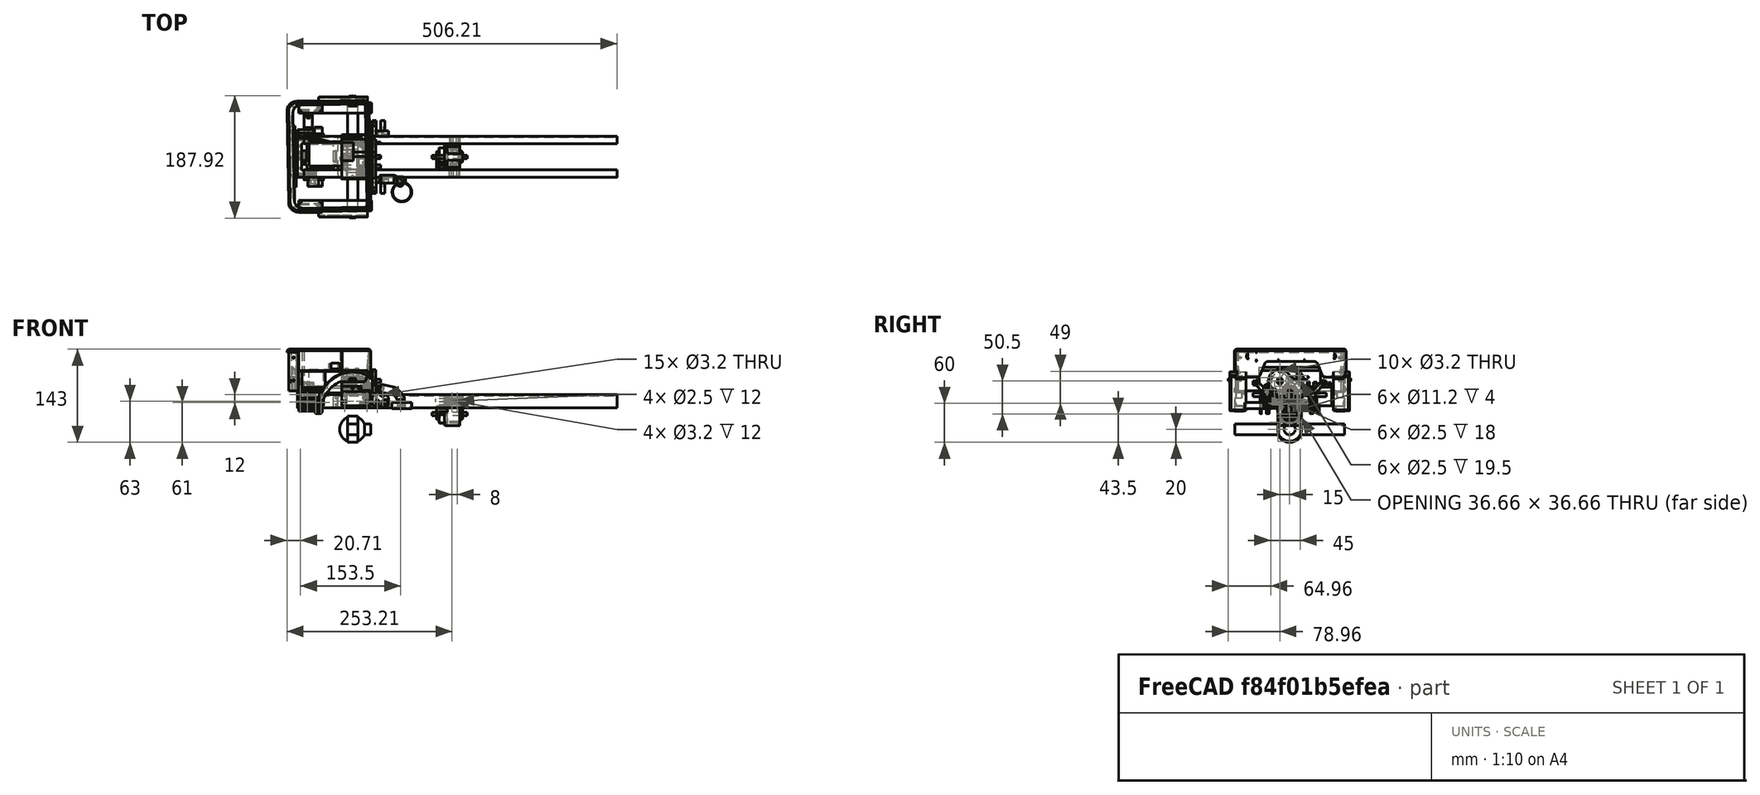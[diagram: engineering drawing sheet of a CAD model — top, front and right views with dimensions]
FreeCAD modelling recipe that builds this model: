
FCSTD DOCUMENT  (FreeCAD 0.18.4R)
Label: gearbox-01
License: All rights reserved
LicenseURL: http://en.wikipedia.org/wiki/All_rights_reserved
objects: Part::Cylinder×79, Part::MultiFuse×46, Part::Cut×41, Part::Box×25, Part::Fillet×25, Part::Chamfer×11, Part::Feature×6, Part::Extrusion×5, Part::Mirroring×4, Part::Sphere×1
note: 243 computed .brp shape members not serialized (recipe doc carries the construction recipe); baked Part::Feature solids carry a one-line shape summary decoded from their .brp

FEATURE [Part::Box] Box416  label="Cube641"
  AttacherType = Attacher::AttachEngine3D
  Height = 20
  Length = 480
  Placement = pos=(0,0,-92) rot=(0,0,1;0rad)
  Width = 11.5
FEATURE [Part::Box] Box417  label="Cube642"
  AttacherType = Attacher::AttachEngine3D
  Height = 17
  Length = 480
  Placement = pos=(0,1.5,-90.5) rot=(0,0,1;0rad)
  Width = 10
FEATURE [Part::Cut] Cut429  label="Cut768"
  Base = -> Box416
  Refine = true
  Tool = -> Box417
FEATURE [Part::Fillet] Fillet268
  Base = -> Cut429
  Edges = 2 edges r=3: [Edge11,Edge23]
  Placement = pos=(0,-1.5,0) rot=(0,0,1;0rad)
FEATURE [Part::Box] Box418  label="Cube643"
  AttacherType = Attacher::AttachEngine3D
  Height = 20
  Length = 480
  Placement = pos=(0,0,-92) rot=(0,0,1;0rad)
  Width = 11.5
FEATURE [Part::Box] Box419  label="Cube644"
  AttacherType = Attacher::AttachEngine3D
  Height = 17
  Length = 480
  Placement = pos=(0,1.5,-90.5) rot=(0,0,1;0rad)
  Width = 10
FEATURE [Part::Cut] Cut430  label="Cut769"
  Base = -> Box418
  Refine = true
  Tool = -> Box419
FEATURE [Part::Fillet] Fillet269
  Base = -> Cut430
  Edges = 2 edges r=3: [Edge11,Edge23]
FEATURE [Part::Mirroring] Part__Mirroring036  label="Fillet269 (Mirror #29)"
  Base = (0,0,0)
  Normal = (0,1,0)
  Placement = pos=(0,61.5,0) rot=(0,0,1;0rad)
  Source = -> Fillet269
FEATURE [Part::MultiFuse] Fusion231  label="frame-00"
  Placement = pos=(23.5,55,74) rot=(0,0,1;0rad)
  Refine = true
  Shapes = -> [Part__Mirroring036,Fillet268]
FEATURE [Part::Box] Box042  label="Cube280"
  AttacherType = Attacher::AttachEngine3D
  Height = 28
  Length = 21
  Placement = pos=(-13,0,0) rot=(0,0,1;0rad)
  Width = 170
FEATURE [Part::Fillet] Fillet013
  Base = -> Box042
  Edges = 2 edges r=15: [Edge1,Edge3]
FEATURE [Part::Box] Box184  label="Cube410"
  AttacherType = Attacher::AttachEngine3D
  Height = 10
  Length = 2.5
  Placement = pos=(-1.25,0,0) rot=(0,0,1;0rad)
  Width = 4
FEATURE [Part::Cylinder] Cylinder068
  Angle = 360
  AttacherType = Attacher::AttachEngine3D
  Height = 10
  Placement = pos=(0,4,0) rot=(0,0,1;0rad)
  Radius = 1.25
FEATURE [Part::Cylinder] Cylinder069
  Angle = 360
  AttacherType = Attacher::AttachEngine3D
  Height = 10
  Radius = 1.25
FEATURE [Part::MultiFuse] Fusion056
  Placement = pos=(0,8,0) rot=(0,0,1;0rad)
  Refine = true
  Shapes = -> [Box184,Cylinder068,Cylinder069]
FEATURE [Part::Cut] Cut014047  label="diff-box-rear-01"
  Placement = pos=(0,0,-1) rot=(0,0,1;0rad)
  Refine = true
FEATURE [Part::Fillet] Fillet355  label="diff-box-front-01"
  Edges = 1 edges r=1.99: [Edge305]
FEATURE [Part::Cylinder] Cylinder088
  Angle = 360
  AttacherType = Attacher::AttachEngine3D
  Height = 43.5
  Placement = pos=(20.75,0,-18.5) rot=(0,0,1;0rad)
  Radius = 2.5
FEATURE [Part::Cylinder] Cylinder087
  Angle = 360
  AttacherType = Attacher::AttachEngine3D
  Height = 54
  Placement = pos=(0,0,-23.5) rot=(0,0,1;0rad)
  Radius = 2.5
FEATURE [Part::Cut] Cut014020  label="diff-box-mount-left"
  Base = -> Fillet013
  Placement = pos=(0,0,-1) rot=(0,0,1;0rad)
  Refine = true
  Tool = -> Fusion056
FEATURE [Part::Mirroring] Part__Mirroring001  label="diff-box-mount-right"
  Base = (0,0,0)
  Normal = (0,1,0)
  Placement = pos=(0,0,-1) rot=(0,0,1;0rad)
FEATURE [Part::MultiFuse] Fusion514  label="transfer-case"
  Placement = pos=(250,85,-27.5) rot=(0,-1,0;1.5708rad)
  Refine = true
  Shapes = -> [Cut014047,Fillet355,Cylinder087,Cylinder088,Cut014020,Part__Mirroring001]
FEATURE [Part::Fillet] Fillet357  label="steering-servo-rear-mount"
  Edges = 4 edges r=3: [Edge11,Edge13,Edge21,Edge23]
  Placement = pos=(1,0,3) rot=(0,0,1;0rad)
FEATURE [Part::Cut] Cut694  label="steering-servo-front-mount"
  Placement = pos=(0,0,3) rot=(0,0,1;0rad)
  Refine = true
FEATURE [Part::MultiFuse] Fusion588  label="steering-servo"
  Placement = pos=(1,0,3) rot=(0,0,1;0rad)
  Refine = true
FEATURE [Part::Cut] Cut688  label="servo-shaft-coupler"
  Placement = pos=(37,58.75,-14.35) rot=(1,0,0;1.5708rad)
  Refine = true
FEATURE [Part::Box] Box498  label="Cube700"
  AttacherType = Attacher::AttachEngine3D
  Height = 16
  Length = 16
  Placement = pos=(90,1,-59) rot=(0,0,1;0rad)
  Width = 168
FEATURE [Part::Cylinder] Cylinder793  label="Cylinder955"
  Angle = 360
  AttacherType = Attacher::AttachEngine3D
  Height = 16
  Placement = pos=(90,85,-51) rot=(0,1,0;1.5708rad)
  Radius = 20
FEATURE [Part::Sphere] Sphere
  Angle1 = -90
  Angle2 = 90
  Angle3 = 360
  AttacherType = Attacher::AttachEngine3D
  Placement = pos=(98,85,-51) rot=(0,0,1;0rad)
  Radius = 20
FEATURE [Part::Cylinder] Cylinder794  label="Cylinder956"
  Angle = 360
  AttacherType = Attacher::AttachEngine3D
  Height = 28
  Placement = pos=(98,85,-51) rot=(0,1,0;1.5708rad)
  Radius = 8.5
FEATURE [Part::MultiFuse] Fusion512  label="front-axle"
  Refine = true
  Shapes = -> [Box498,Sphere,Cylinder794,Cylinder793]
FEATURE [Part::Cylinder] Cylinder
  Angle = 360
  AttacherType = Attacher::AttachEngine3D
  Height = 39.5
  Placement = pos=(0,0,23) rot=(0,1,0;1.5708rad)
  Radius = 13
FEATURE [Part::Cylinder] Cylinder795
  Angle = 360
  AttacherType = Attacher::AttachEngine3D
  Height = 39.5
  Placement = pos=(0,0,0) rot=(0,1,0;1.5708rad)
  Radius = 19.5
FEATURE [Part::Cylinder] Cylinder798  label="cylinder"
  Angle = 360
  AttacherType = Attacher::AttachEngine3D
  Height = 50
  Placement = pos=(31,89,23) rot=(0,1,0;1.5708rad)
  Radius = 18
FEATURE [Part::MultiFuse] Fusion  label="gearbox002"
  Placement = pos=(89,84.9373,3.51066) rot=(1,0,0;0.706858rad)
  Refine = true
  Shapes = -> [Cylinder,Cylinder795]
FEATURE [Part::Box] Box  label="Cube"
  AttacherType = Attacher::AttachEngine3D
  Height = 41
  Length = 47.5
  Placement = pos=(81,65,-17) rot=(0,0,1;0rad)
  Width = 40
FEATURE [Part::Cylinder] Cylinder799
  Angle = 360
  AttacherType = Attacher::AttachEngine3D
  Height = 60
  Placement = pos=(81,85,3.5) rot=(0,1,0;1.5708rad)
  Radius = 2.5
FEATURE [Part::Cylinder] Cylinder800
  Angle = 360
  AttacherType = Attacher::AttachEngine3D
  Height = 60
  Placement = pos=(81,70,21) rot=(0,1,0;1.5708rad)
  Radius = 2.5
FEATURE [Part::MultiFuse] Fusion590
  Refine = true
  Shapes = -> [Cylinder799,Cylinder800]
FEATURE [Part::Cylinder] Cylinder801  label="main-motor001"
  Angle = 360
  AttacherType = Attacher::AttachEngine3D
  Height = 18
  Placement = pos=(81,89,21) rot=(0,1,0;1.5708rad)
  Radius = 18
FEATURE [Part::Cylinder] Cylinder802
  Angle = 360
  AttacherType = Attacher::AttachEngine3D
  Height = 47.5
  Placement = pos=(81,70,21) rot=(0,1,0;1.5708rad)
  Radius = 17.5
FEATURE [Part::Cylinder] Cylinder804
  Angle = 360
  AttacherType = Attacher::AttachEngine3D
  Height = 60
  Placement = pos=(81,106.419,11.8645) rot=(0.034878,0.998783,0.034878;1.57201rad)
  Radius = 1.5
FEATURE [Part::Feature] Fillet007001  label="selector"
  Placement = pos=(119.5,85,5.5) rot=(0.181732,-0.966409,-0.181732;1.60496rad)
  shape: bbox 10 x 30 x 28.57 mm, 21 faces (baked)
FEATURE [Part::Box] Box499  label="Cube701"
  AttacherType = Attacher::AttachEngine3D
  Height = 22
  Length = 47.5
  Placement = pos=(81,105,2) rot=(0,0,1;0rad)
  Width = 7
FEATURE [Part::MultiFuse] Fusion591
  Refine = true
  Shapes = -> [Box499,Cylinder802,Box,Cylinder801]
FEATURE [Part::Cylinder] Cylinder805
  Angle = 360
  AttacherType = Attacher::AttachEngine3D
  Height = 10
  Placement = pos=(89,70,21) rot=(0,1,0;1.5708rad)
  Radius = 16.5
FEATURE [Part::MultiFuse] Fusion592
  Refine = true
  Shapes = -> [Fusion,Cylinder805]
FEATURE [Part::Cut] Cut
  Base = -> Fusion591
  Refine = true
  Tool = -> Fusion592
FEATURE [Part::Chamfer] Chamfer
  Base = -> Cut
  Edges = 1 edges r=3.49: [Edge39]
FEATURE [Part::Fillet] Fillet
  Base = -> Chamfer
  Edges = 1 edges r=3: [Edge25]
FEATURE [Part::Fillet] Fillet007002
  Base = -> Fillet
  Edges = 2 edges r=6: [Edge13,Edge18]
FEATURE [Part::Box] Box500  label="Cube702"
  AttacherType = Attacher::AttachEngine3D
  Height = 20
  Length = 60
  Placement = pos=(81,53.25,-18) rot=(0,0,1;0rad)
  Width = 63.5
FEATURE [Part::Feature] Face
  shape: bbox 2.621e-05 x 37.61 x 40.07 mm, 1 faces, 0 solids (baked)
FEATURE [Part::Extrusion] Extrude
  Base = -> Face
  Dir = (60,0,0)
  DirMode = 0
  FaceMakerClass = Part::FaceMakerExtrusion
  LengthFwd = 0
  LengthRev = 0
  Placement = pos=(-30.4,1.43133,-5.60163) rot=(1,0,0;0.069813rad)
  Solid = false
  Symmetric = false
FEATURE [Part::Cylinder] Cylinder806
  Angle = 360
  AttacherType = Attacher::AttachEngine3D
  Height = 60
  Placement = pos=(81,106.419,11.8645) rot=(0.034878,0.998783,0.034878;1.57201rad)
  Radius = 3.1
FEATURE [Part::Cut] Cut014049
  Base = -> Fillet007002
  Refine = true
  Tool = -> Extrude
FEATURE [Part::Cut] Cut014050
  Base = -> Cut014049
  Refine = true
  Tool = -> Cylinder806
FEATURE [Part::Cylinder] Cylinder807  label="Cylinder000"
  Angle = 360
  AttacherType = Attacher::AttachEngine3D
  Height = 50
  Placement = pos=(45,89,21) rot=(0,1,0;1.5708rad)
  Radius = 7
FEATURE [Part::Cut] Cut014051
  Base = -> Cut014050
  Refine = true
  Tool = -> Cylinder807
FEATURE [Part::Chamfer] Chamfer109
  Base = -> Cut014051
  Edges = 1 edges r=5.2: [Edge52]
FEATURE [Part::Cylinder] Cylinder808  label="Cylinder957"
  Angle = 360
  AttacherType = Attacher::AttachEngine3D
  Height = 50
  Placement = pos=(56,89,33.5) rot=(0,1,0;1.5708rad)
  Radius = 1.6
FEATURE [Part::Cylinder] Cylinder809  label="Cylinder958"
  Angle = 360
  AttacherType = Attacher::AttachEngine3D
  Height = 50
  Placement = pos=(56,89,8.5) rot=(0,1,0;1.5708rad)
  Radius = 1.6
FEATURE [Part::MultiFuse] Fusion593
  Placement = pos=(0,14.7618,74.3919) rot=(-1,0,0;0.855211rad)
  Refine = true
  Shapes = -> [Cylinder808,Cylinder809]
FEATURE [Part::Cylinder] Cylinder810  label="Cylinder959"
  Angle = 360
  AttacherType = Attacher::AttachEngine3D
  Height = 15
  Placement = pos=(56,89,33.5) rot=(0,1,0;1.5708rad)
  Radius = 3.1
FEATURE [Part::Cylinder] Cylinder811  label="Cylinder960"
  Angle = 360
  AttacherType = Attacher::AttachEngine3D
  Height = 15
  Placement = pos=(56,89,8.5) rot=(0,1,0;1.5708rad)
  Radius = 3.1
FEATURE [Part::MultiFuse] Fusion594
  Placement = pos=(28,14.7618,74.3919) rot=(-1,0,0;0.855211rad)
  Refine = true
  Shapes = -> [Cylinder810,Cylinder811]
FEATURE [Part::MultiFuse] Fusion595
  Refine = true
  Shapes = -> [Fusion593,Fusion594]
FEATURE [Part::Cut] Cut014052
  Base = -> Chamfer109
  Refine = true
  Tool = -> Fusion595
FEATURE [Part::Cylinder] Cylinder812
  Angle = 360
  AttacherType = Attacher::AttachEngine3D
  Height = 60
  Placement = pos=(81,85,3.5) rot=(0,1,0;1.5708rad)
  Radius = 5.6
FEATURE [Part::Cylinder] Cylinder813
  Angle = 360
  AttacherType = Attacher::AttachEngine3D
  Height = 60
  Placement = pos=(81,70,21) rot=(0,1,0;1.5708rad)
  Radius = 5.6
FEATURE [Part::MultiFuse] Fusion596
  Placement = pos=(4,0,0) rot=(0,0,1;0rad)
  Refine = true
  Shapes = -> [Cylinder812,Cylinder813]
FEATURE [Part::Cylinder] Cylinder814
  Angle = 360
  AttacherType = Attacher::AttachEngine3D
  Height = 60
  Placement = pos=(81,85,3.5) rot=(0,1,0;1.5708rad)
  Radius = 4
FEATURE [Part::Cylinder] Cylinder815
  Angle = 360
  AttacherType = Attacher::AttachEngine3D
  Height = 60
  Placement = pos=(81,70,21) rot=(0,1,0;1.5708rad)
  Radius = 4
FEATURE [Part::MultiFuse] Fusion597
  Refine = true
  Shapes = -> [Cylinder814,Cylinder815]
FEATURE [Part::MultiFuse] Fusion598
  Refine = true
  Shapes = -> [Fusion596,Fusion597]
FEATURE [Part::Cut] Cut014053
  Base = -> Cut014052
  Refine = true
  Tool = -> Fusion598
FEATURE [Part::Cylinder] Cylinder816
  Angle = 360
  AttacherType = Attacher::AttachEngine3D
  Height = 20
  Placement = pos=(81,69,-13) rot=(0,1,0;1.5708rad)
  Radius = 1.25
FEATURE [Part::Cylinder] Cylinder817
  Angle = 360
  AttacherType = Attacher::AttachEngine3D
  Height = 20
  Placement = pos=(81,101,-13) rot=(0,1,0;1.5708rad)
  Radius = 1.25
FEATURE [Part::Cylinder] Cylinder818
  Angle = 360
  AttacherType = Attacher::AttachEngine3D
  Height = 20
  Placement = pos=(81,101,21) rot=(0,1,0;1.5708rad)
  Radius = 1.25
FEATURE [Part::Cylinder] Cylinder819
  Angle = 360
  AttacherType = Attacher::AttachEngine3D
  Height = 20
  Placement = pos=(81,70,36) rot=(0,1,0;1.5708rad)
  Radius = 1.25
FEATURE [Part::Cylinder] Cylinder820
  Angle = 360
  AttacherType = Attacher::AttachEngine3D
  Height = 20
  Placement = pos=(81,56,26) rot=(0,1,0;1.5708rad)
  Radius = 1.25
FEATURE [Part::Cylinder] Cylinder821
  Angle = 360
  AttacherType = Attacher::AttachEngine3D
  Height = 20
  Placement = pos=(81,62,8) rot=(0,1,0;1.5708rad)
  Radius = 1.25
FEATURE [Part::MultiFuse] Fusion599
  Placement = pos=(28,0,0) rot=(0,0,1;0rad)
  Refine = true
  Shapes = -> [Cylinder816,Cylinder820,Cylinder821,Cylinder817,Cylinder818,Cylinder819]
FEATURE [Part::Cut] Cut014054
  Base = -> Cut014053
  Placement = pos=(0,0,2) rot=(0,0,1;0rad)
  Refine = true
  Tool = -> Fusion599
FEATURE [Part::Box] Box501  label="Cube703"
  AttacherType = Attacher::AttachEngine3D
  Height = 22
  Length = 44
  Placement = pos=(81,51,-15) rot=(0,0,1;0rad)
  Width = 14
FEATURE [Part::Fillet] Fillet007003
  Base = -> Box500
  Edges = 2 edges r=3: [Edge10,Edge12]
FEATURE [Part::Box] Box502  label="Cube704"
  AttacherType = Attacher::AttachEngine3D
  Height = 22
  Length = 44
  Placement = pos=(81,105,-15) rot=(0,0,1;0rad)
  Width = 14
FEATURE [Part::Cylinder] Cylinder822  label="Cylinder961"
  Angle = 360
  AttacherType = Attacher::AttachEngine3D
  Height = 5
  Placement = pos=(120,125,-8) rot=(1,0,0;1.5708rad)
  Radius = 1.6
FEATURE [Part::Cylinder] Cylinder823  label="Cylinder962"
  Angle = 360
  AttacherType = Attacher::AttachEngine3D
  Height = 5
  Placement = pos=(86,125,-8) rot=(1,0,0;1.5708rad)
  Radius = 1.6
FEATURE [Part::MultiFuse] Fusion603
  Placement = pos=(0,-5,0) rot=(0,0,1;0rad)
  Refine = true
  Shapes = -> [Cylinder823,Cylinder822]
FEATURE [Part::Cylinder] Cylinder824  label="Cylinder963"
  Angle = 360
  AttacherType = Attacher::AttachEngine3D
  Height = 5
  Placement = pos=(120,125,-8) rot=(1,0,0;1.5708rad)
  Radius = 1.6
FEATURE [Part::Cylinder] Cylinder825  label="Cylinder964"
  Angle = 360
  AttacherType = Attacher::AttachEngine3D
  Height = 5
  Placement = pos=(86,125,-8) rot=(1,0,0;1.5708rad)
  Radius = 1.6
FEATURE [Part::MultiFuse] Fusion604
  Placement = pos=(0,-70,0) rot=(0,0,1;0rad)
  Refine = true
  Shapes = -> [Cylinder825,Cylinder824]
FEATURE [Part::MultiFuse] Fusion605
  Refine = true
  Shapes = -> [Fusion603,Fusion604]
FEATURE [Part::Feature] Face044
  shape: bbox 2e-07 x 80.32 x 83.91 mm, 1 faces, 0 solids (baked)
FEATURE [Part::Extrusion] Extrude001
  Base = -> Face044
  Dir = (5,0,0)
  DirMode = 0
  FaceMakerClass = Part::FaceMakerExtrusion
  LengthFwd = 0
  LengthRev = 0
  Solid = false
  Symmetric = false
FEATURE [Part::Cylinder] Cylinder826
  Angle = 360
  AttacherType = Attacher::AttachEngine3D
  Height = 60
  Placement = pos=(81,85,3.5) rot=(0,1,0;1.5708rad)
  Radius = 4
FEATURE [Part::Cylinder] Cylinder827
  Angle = 360
  AttacherType = Attacher::AttachEngine3D
  Height = 60
  Placement = pos=(81,70,21) rot=(0,1,0;1.5708rad)
  Radius = 4
FEATURE [Part::MultiFuse] Fusion606
  Refine = true
  Shapes = -> [Cylinder826,Cylinder827]
FEATURE [Part::Cylinder] Cylinder828
  Angle = 360
  AttacherType = Attacher::AttachEngine3D
  Height = 60
  Placement = pos=(81,85,3.5) rot=(0,1,0;1.5708rad)
  Radius = 5.6
FEATURE [Part::Cylinder] Cylinder829
  Angle = 360
  AttacherType = Attacher::AttachEngine3D
  Height = 60
  Placement = pos=(81,70,21) rot=(0,1,0;1.5708rad)
  Radius = 5.6
FEATURE [Part::MultiFuse] Fusion607
  Placement = pos=(-8.5,0,0) rot=(0,0,1;0rad)
  Refine = true
  Shapes = -> [Cylinder828,Cylinder829]
FEATURE [Part::MultiFuse] Fusion608
  Refine = true
  Shapes = -> [Fusion607,Fusion606]
FEATURE [Part::Cut] Cut014057
  Base = -> Extrude001
  Refine = true
  Tool = -> Fusion608
FEATURE [Part::Cylinder] Cylinder830
  Angle = 360
  AttacherType = Attacher::AttachEngine3D
  Height = 60
  Placement = pos=(81,106.419,11.8645) rot=(0.034878,0.998783,0.034878;1.57201rad)
  Radius = 3.1
FEATURE [Part::Cut] Cut014058
  Base = -> Cut014057
  Refine = true
  Tool = -> Cylinder830
FEATURE [Part::Cylinder] Cylinder831
  Angle = 360
  AttacherType = Attacher::AttachEngine3D
  Height = 20
  Placement = pos=(81,69,-13) rot=(0,1,0;1.5708rad)
  Radius = 1.6
FEATURE [Part::Cylinder] Cylinder832
  Angle = 360
  AttacherType = Attacher::AttachEngine3D
  Height = 20
  Placement = pos=(81,101,-13) rot=(0,1,0;1.5708rad)
  Radius = 1.6
FEATURE [Part::Cylinder] Cylinder833
  Angle = 360
  AttacherType = Attacher::AttachEngine3D
  Height = 20
  Placement = pos=(81,101,21) rot=(0,1,0;1.5708rad)
  Radius = 1.6
FEATURE [Part::Cylinder] Cylinder834
  Angle = 360
  AttacherType = Attacher::AttachEngine3D
  Height = 20
  Placement = pos=(81,70,36) rot=(0,1,0;1.5708rad)
  Radius = 1.6
FEATURE [Part::Cylinder] Cylinder835
  Angle = 360
  AttacherType = Attacher::AttachEngine3D
  Height = 20
  Placement = pos=(81,56,26) rot=(0,1,0;1.5708rad)
  Radius = 1.6
FEATURE [Part::Cylinder] Cylinder836
  Angle = 360
  AttacherType = Attacher::AttachEngine3D
  Height = 20
  Placement = pos=(81,62,8) rot=(0,1,0;1.5708rad)
  Radius = 1.6
FEATURE [Part::MultiFuse] Fusion609
  Placement = pos=(40,0,2) rot=(0,0,1;0rad)
  Refine = true
  Shapes = -> [Cylinder831,Cylinder835,Cylinder836,Cylinder832,Cylinder833,Cylinder834]
FEATURE [Part::Box] Box504  label="Cube706"
  AttacherType = Attacher::AttachEngine3D
  Height = 10
  Length = 30
  Placement = pos=(81,111,5) rot=(0,0,1;0rad)
  Width = 5.5
FEATURE [Part::MultiFuse] Fusion610  label="gearbox-rods"
  Placement = pos=(0,0,2) rot=(0,0,1;0rad)
  Refine = true
  Shapes = -> [Cylinder804,Fusion590]
FEATURE [Part::Chamfer] Chamfer110
  Base = -> Box502
  Edges = 1 edges r=2: [Edge10]
FEATURE [Part::MultiFuse] Fusion611
  Refine = true
  Shapes = -> [Box501,Chamfer110]
FEATURE [Part::Cut] Cut014060
  Base = -> Fusion611
  Refine = true
  Tool = -> Fillet007003
FEATURE [Part::MultiFuse] Fusion612
  Refine = true
  Shapes = -> [Cut014054,Cut014060]
FEATURE [Part::Fillet] Fillet007004
  Base = -> Fusion612
  Edges = 1 edges r=4: [Edge94]
FEATURE [Part::Fillet] Fillet007005
  Base = -> Fillet007004
  Edges = 2 edges r=4: [Edge124,Edge131]
FEATURE [Part::Chamfer] Chamfer111
  Base = -> Fillet007005
  Edges = 1 edges r=3: [Edge58]
FEATURE [Part::Fillet] Fillet007006
  Base = -> Chamfer111
  Edges = 1 edges r=2: [Edge92]
FEATURE [Part::Fillet] Fillet007007
  Base = -> Cut014058
  Edges = 1 edges r=2: [Edge1]
FEATURE [Part::Fillet] Fillet007008
  Base = -> Fillet007007
  Edges = 1 edges r=3: [Edge41]
  Placement = pos=(0,0,2) rot=(0,0,1;0rad)
FEATURE [Part::Fillet] Fillet007009
  Base = -> Fillet007006
  Edges = 1 edges r=2.99: [Edge67]
FEATURE [Part::Cylinder] Cylinder837  label="Cylinder965"
  Angle = 360
  AttacherType = Attacher::AttachEngine3D
  Height = 10
  Placement = pos=(96,125,-8) rot=(1,0,0;1.5708rad)
  Radius = 1.25
FEATURE [Part::Cylinder] Cylinder838  label="Cylinder966"
  Angle = 360
  AttacherType = Attacher::AttachEngine3D
  Height = 10
  Placement = pos=(86,125,-8) rot=(1,0,0;1.5708rad)
  Radius = 1.25
FEATURE [Part::MultiFuse] Fusion613
  Placement = pos=(12,-3.5,20) rot=(0,0,1;0rad)
  Refine = true
  Shapes = -> [Cylinder838,Cylinder837]
FEATURE [Part::Cylinder] Cylinder839  label="Cylinder967"
  Angle = 360
  AttacherType = Attacher::AttachEngine3D
  Height = 8
  Placement = pos=(96,124,-8) rot=(1,0,0;1.5708rad)
  Radius = 1.25
FEATURE [Part::Cylinder] Cylinder840  label="Cylinder968"
  Angle = 360
  AttacherType = Attacher::AttachEngine3D
  Height = 8
  Placement = pos=(86,120.5,-8) rot=(1,0,0;1.5708rad)
  Radius = 1.25
FEATURE [Part::Box] Box505  label="Cube707"
  AttacherType = Attacher::AttachEngine3D
  Height = 10
  Length = 30
  Placement = pos=(95,53.5,5) rot=(0,0,1;0rad)
  Width = 7
FEATURE [Part::Chamfer] Chamfer112
  Base = -> Box505
  Edges = 1 edges r=6: [Edge12]
  Placement = pos=(-14,0,0) rot=(0,0,1;0rad)
FEATURE [Part::Fillet] Fillet007010
  Base = -> Box504
  Edges = 1 edges r=1: [Edge12]
FEATURE [Part::Fillet] Fillet007011
  Base = -> Chamfer112
  Edges = 1 edges r=0.99: [Edge7]
FEATURE [Part::MultiFuse] Fusion616
  Refine = true
  Shapes = -> [Fillet007009,Fillet007011,Fillet007010]
FEATURE [Part::MultiFuse] Fusion614
  Placement = pos=(12,-64,20) rot=(0,0,1;0rad)
  Refine = true
  Shapes = -> [Cylinder840,Cylinder839]
FEATURE [Part::MultiFuse] Fusion617
  Refine = true
  Shapes = -> [Fusion613,Fusion614]
FEATURE [Part::MultiFuse] Fusion618
  Refine = true
  Shapes = -> [Fusion605,Fusion617]
FEATURE [Part::Fillet] Fillet007012
  Base = -> Fusion616
  Edges = 2 edges r=6: [Edge81,Edge92]
FEATURE [Part::Box] Box506  label="Cube708"
  AttacherType = Attacher::AttachEngine3D
  Height = 2
  Length = 39.5
  Placement = pos=(89,104,2) rot=(1,0,0;1.0821rad)
  Width = 10
FEATURE [Part::Box] Box507  label="Cube709"
  AttacherType = Attacher::AttachEngine3D
  Height = 2
  Length = 39.5
  Placement = pos=(89,96,19) rot=(-1,0,0;0.314159rad)
  Width = 10
FEATURE [Part::MultiFuse] Fusion619
  Refine = true
  Shapes = -> [Box507,Box506]
FEATURE [Part::Cut] Cut014062
  Base = -> Fillet007012
  Refine = true
  Tool = -> Fusion619
FEATURE [Part::Cylinder] Cylinder841
  Angle = 360
  AttacherType = Attacher::AttachEngine3D
  Height = 19
  Placement = pos=(89,70,23) rot=(0,1,0;1.5708rad)
  Radius = 16.5
FEATURE [Part::Chamfer] Chamfer113
  Base = -> Cylinder841
  Edges = 1 edges r=4: [Edge1]
FEATURE [Part::Box] Box508  label="Cube710"
  AttacherType = Attacher::AttachEngine3D
  Height = 32
  Length = 19
  Placement = pos=(89,70,7) rot=(0,0,1;0rad)
  Width = 32
FEATURE [Part::Chamfer] Chamfer114
  Base = -> Box508
  Edges = 2 edges r=4: [Edge6,Edge8]
  Placement = pos=(0,5.43898,58.5088) rot=(-1,0,0;0.820305rad)
FEATURE [Part::Chamfer] Chamfer115
  Base = -> Cut014062
  Edges = 1 edges r=5: [Edge65]
FEATURE [Part::MultiFuse] Fusion620
  Refine = true
  Shapes = -> [Chamfer113,Chamfer114]
FEATURE [Part::Cut] Cut014063
  Base = -> Chamfer115
  Refine = true
  Tool = -> Fusion620
FEATURE [Part::Cut] Cut014064  label="gearbox-front"
  Base = -> Cut014063
  Refine = true
  Tool = -> Fusion618
FEATURE [Part::Chamfer] Chamfer116
  Base = -> Fillet007008
  Edges = 1 edges r=5: [Edge35]
FEATURE [Part::Cut] Cut014065  label="gearbox-rear"
  Base = -> Chamfer116
  Refine = true
  Tool = -> Fusion609
FEATURE [Part::Cut] Cut700  label="cross-member-front"
  Placement = pos=(0,0,3) rot=(0,0,1;0rad)
  Refine = true
FEATURE [Part::Chamfer] Chamfer162  label="air-box-holder"
  Edges = 1 edges r=1.49: [Edge71]
FEATURE [Part::Fillet] Fillet007067  label="wing-support-left"
  Edges = 1 edges r=3: [Edge15]
FEATURE [Part::Mirroring] Part__Mirroring114  label="wing-support-right"
  Base = (0,0,0)
  Normal = (0,1,0)
  Placement = pos=(0,170,0) rot=(0,0,1;0rad)
FEATURE [Part::Cylinder] Cylinder843  label="Cylinder969"
  Angle = 360
  AttacherType = Attacher::AttachEngine3D
  Height = 68
  Placement = pos=(66,106.5,14) rot=(0,1,0;1.5708rad)
  Radius = 1.5
FEATURE [Part::MultiFuse] Fusion563  label="leafspring-mount-front-left-int-servo"
  Placement = pos=(0,0,3) rot=(0,0,1;0rad)
  Refine = true
FEATURE [Part::Mirroring] Part__Mirroring105  label="leafspring-mount-front-right"
  Base = (0,0,0)
  Normal = (0,1,0)
  Placement = pos=(0,170,0) rot=(0,0,1;0rad)
FEATURE [Part::Cut] Cut398  label="cab-lower-part-05"
  Placement = pos=(0,0,8) rot=(0,0,1;0.017453rad)
  Refine = true
FEATURE [Part::Cut] Cut408  label="left-wing-01"
  Placement = pos=(0,0,8) rot=(0,0,1;0rad)
  Refine = true
FEATURE [Part::Cut] Cut409  label="right-wing-01"
  Placement = pos=(0,0,8) rot=(0,0,1;0rad)
  Refine = true
FEATURE [Part::Cylinder] Cylinder844  label="Cylinder970"
  Angle = 360
  AttacherType = Attacher::AttachEngine3D
  Height = 15
  Placement = pos=(31,111.5,14) rot=(0,1,0;1.5708rad)
  Radius = 1.5
FEATURE [Part::Cut] Cut014188  label="hitec-hs85bb"
  Placement = pos=(23.5,149.5,14) rot=(0.57735,0.57735,-0.57735;2.0944rad)
  Refine = true
FEATURE [Part::Cut] Cut014189  label="cross-member-front001"
  Placement = pos=(0,0,3) rot=(0,0,1;0rad)
  Refine = true
FEATURE [Part::Box] Box509  label="Cube711"
  AttacherType = Attacher::AttachEngine3D
  Height = 7
  Length = 23
  Placement = pos=(14,116.5,-24.5) rot=(0,0,1;0rad)
  Width = 10
FEATURE [Part::Box] Box510  label="Cube712"
  AttacherType = Attacher::AttachEngine3D
  Height = 44
  Length = 10
  Placement = pos=(14,116.5,-24.5) rot=(0,0,1;0rad)
  Width = 10
FEATURE [Part::Box] Box511  label="Cube713"
  AttacherType = Attacher::AttachEngine3D
  Height = 7
  Length = 23
  Placement = pos=(14,116.5,12.5) rot=(0,0,1;0rad)
  Width = 10
FEATURE [Part::Box] Box512  label="Cube714"
  AttacherType = Attacher::AttachEngine3D
  Height = 7
  Length = 22
  Placement = pos=(17,111.5,12.5) rot=(0,0,1;0rad)
  Width = 10
FEATURE [Part::MultiFuse] Fusion621
  Refine = true
  Shapes = -> [Box511,Box509,Box510]
FEATURE [Part::Cut] Cut014190
  Base = -> Fusion621
  Placement = pos=(-0.5,0,0) rot=(0,0,1;0rad)
  Refine = true
  Tool = -> Box512
FEATURE [Part::Box] Box513  label="Cube715"
  AttacherType = Attacher::AttachEngine3D
  Height = 17
  Length = 1
  Placement = pos=(13.5,113.5,4.5) rot=(0,0,1;0rad)
  Width = 13
FEATURE [Part::Cylinder] Cylinder845  label="Cylinder971"
  Angle = 360
  AttacherType = Attacher::AttachEngine3D
  Height = 10
  Placement = pos=(18,116.5,2) rot=(-1,0,0;1.5708rad)
  Radius = 1.6
FEATURE [Part::Cylinder] Cylinder846  label="Cylinder972"
  Angle = 360
  AttacherType = Attacher::AttachEngine3D
  Height = 10
  Placement = pos=(18,116.5,-9) rot=(-1,0,0;1.5708rad)
  Radius = 1.6
FEATURE [Part::Box] Box514  label="Cube716"
  AttacherType = Attacher::AttachEngine3D
  Height = 31.5
  Length = 9
  Placement = pos=(13.5,113.5,-24.5) rot=(0,0,1;0rad)
  Width = 10
FEATURE [Part::MultiFuse] Fusion622
  Refine = true
  Shapes = -> [Box514,Cut014190]
FEATURE [Part::Cylinder] Cylinder847  label="Cylinder973"
  Angle = 360
  AttacherType = Attacher::AttachEngine3D
  Height = 10
  Placement = pos=(30,116.5,17.15) rot=(-1,0,0;1.5708rad)
  Radius = 0.9
FEATURE [Part::Cylinder] Cylinder848  label="Cylinder974"
  Angle = 360
  AttacherType = Attacher::AttachEngine3D
  Height = 10
  Placement = pos=(30,116.5,-18.15) rot=(-1,0,0;1.5708rad)
  Radius = 0.9
FEATURE [Part::MultiFuse] Fusion623
  Refine = true
  Shapes = -> [Cylinder845,Cylinder846,Cylinder847,Cylinder848]
FEATURE [Part::Box] Box515  label="Cube717"
  AttacherType = Attacher::AttachEngine3D
  Height = 5
  Length = 3
  Placement = pos=(14.5,116.5,14.5) rot=(0,0,1;0rad)
  Width = 5
FEATURE [Part::Box] Box516  label="Cube718"
  AttacherType = Attacher::AttachEngine3D
  Height = 44
  Length = 2
  Placement = pos=(36.5,121.5,-24.5) rot=(0,0,1;0rad)
  Width = 5
FEATURE [Part::MultiFuse] Fusion624
  Placement = pos=(0,0,2) rot=(0,0,1;0rad)
  Refine = true
  Shapes = -> [Fusion622,Box516]
FEATURE [Part::Cut] Cut014191
  Base = -> Fusion624
  Refine = true
  Tool = -> Box513
FEATURE [Part::Cut] Cut014192
  Base = -> Cut014191
  Refine = true
  Tool = -> Cut014189
FEATURE [Part::Cut] Cut014193
  Base = -> Cut014192
  Refine = true
  Tool = -> Fusion623
FEATURE [Part::Fillet] Fillet007068
  Base = -> Cut014193
  Edges = 2 edges r=8.99: [Edge14,Edge33]
FEATURE [Part::Cut] Cut014194
  Base = -> Fillet007068
  Refine = true
  Tool = -> Box515
FEATURE [Part::Chamfer] Chamfer163
  Base = -> Cut014194
  Edges = 1 edges r=6: [Edge62]
FEATURE [Part::Cylinder] Cylinder849  label="Cylinder975"
  Angle = 360
  AttacherType = Attacher::AttachEngine3D
  Height = 21
  Placement = pos=(45.5,111.5,14) rot=(0.242536,0.970143,0;1.5708rad)
  Radius = 1.5
FEATURE [Part::MultiFuse] Fusion625  label="selector-axle"
  Refine = true
  Shapes = -> [Cylinder849,Cylinder844,Cylinder843]
FEATURE [Part::Cylinder] Cylinder009
  Angle = 32.74
  AttacherType = Attacher::AttachEngine3D
  Height = 2.5
  Radius = 10.5
FEATURE [Part::Cylinder] Cylinder010
  Angle = 32.74
  AttacherType = Attacher::AttachEngine3D
  Height = 2.5
  Radius = 7.1
FEATURE [Part::Cylinder] Cylinder011
  Angle = 32.74
  AttacherType = Attacher::AttachEngine3D
  Height = 2.5
  Radius = 10
FEATURE [Part::Cylinder] Cylinder012
  Angle = 32.74
  AttacherType = Attacher::AttachEngine3D
  Height = 2.5
  Radius = 6.9
FEATURE [Part::Cut] Cut007
  Base = -> Cylinder011
  Placement = pos=(0,0,-2.5) rot=(0,0,1;0.244346rad)
  Refine = true
  Tool = -> Cylinder012
FEATURE [Part::Cylinder] Cylinder013
  Angle = 32.74
  AttacherType = Attacher::AttachEngine3D
  Height = 2.5
  Radius = 10
FEATURE [Part::Cylinder] Cylinder014
  Angle = 32.74
  AttacherType = Attacher::AttachEngine3D
  Height = 2.5
  Radius = 6.9
FEATURE [Part::Cut] Cut008
  Base = -> Cylinder013
  Placement = pos=(0,0,-2.5) rot=(0,0,1;0.244346rad)
  Refine = true
  Tool = -> Cylinder014
FEATURE [Part::Cylinder] Cylinder015
  Angle = 360
  AttacherType = Attacher::AttachEngine3D
  Height = 11
  Placement = pos=(0,-8.75,-2.5) rot=(0,0,1;0rad)
  Radius = 0.9
FEATURE [Part::Cylinder] Cylinder017
  Angle = 360
  AttacherType = Attacher::AttachEngine3D
  Height = 11
  Placement = pos=(7.57772,4.375,-2.5) rot=(0,0,1;2.0944rad)
  Radius = 0.9
FEATURE [Part::Cylinder] Cylinder019
  Angle = 360
  AttacherType = Attacher::AttachEngine3D
  Height = 11
  Placement = pos=(-7.57772,4.375,-2.5) rot=(0,0,1;4.18879rad)
  Radius = 0.9
FEATURE [Part::Cut] Cut006
  Base = -> Cylinder009
  Placement = pos=(0,0,-2.5) rot=(0,0,1;0.244346rad)
  Refine = true
  Tool = -> Cylinder010
FEATURE [Part::Feature] Face045
  shape: bbox 18.03 x 18.03 x 2e-07 mm, 1 faces, 0 solids (baked)
FEATURE [Part::Cylinder] Cylinder850
  Angle = 360
  AttacherType = Attacher::AttachEngine3D
  Height = 2
  Radius = 13.5
FEATURE [Part::Cylinder] Cylinder001
  Angle = 360
  AttacherType = Attacher::AttachEngine3D
  Height = 2
  Placement = pos=(0,0,2) rot=(0,0,1;0rad)
  Radius = 11.5
FEATURE [Part::Fillet] Fillet005
  Base = -> Cut008
  Edges = 4 edges r=1.2: [Edge2,Edge4,Edge9,Edge12]
  Placement = pos=(0,0,8.5) rot=(0,0,1;4.18879rad)
FEATURE [Part::MultiFuse] Fusion002
  Placement = pos=(0,0,0.5) rot=(0,0,1;0rad)
  Refine = true
  Shapes = -> [Cylinder015,Cylinder017,Cylinder019]
FEATURE [Part::Fillet] Fillet004
  Base = -> Cut007
  Edges = 4 edges r=1.2: [Edge2,Edge4,Edge9,Edge12]
  Placement = pos=(0,0,8.5) rot=(0,0,1;2.0944rad)
FEATURE [Part::Cylinder] Cylinder002
  Angle = 360
  AttacherType = Attacher::AttachEngine3D
  Height = 2
  Placement = pos=(0,0,4) rot=(0,0,1;0rad)
  Radius = 13.5
FEATURE [Part::Feature] Face002
  shape: bbox 18.03 x 18.03 x 2e-07 mm, 1 faces, 0 solids (baked)
FEATURE [Part::Extrusion] Extrude002
  Base = -> Face045
  Dir = (0,0,6)
  DirMode = 0
  FaceMakerClass = Part::FaceMakerExtrusion
  LengthFwd = 0
  LengthRev = 0
  Solid = false
  Symmetric = false
FEATURE [Part::Cut] Cut014195
  Base = -> Cylinder001
  Refine = true
  Tool = -> Extrude002
FEATURE [Part::Fillet] Fillet003
  Base = -> Cut006
  Edges = 4 edges r=1.5: [Edge2,Edge4,Edge9,Edge12]
  Placement = pos=(0,0,0) rot=(0,0,1;4.18879rad)
FEATURE [Part::Extrusion] Extrude003
  Base = -> Face002
  Dir = (0,0,6)
  DirMode = 0
  FaceMakerClass = Part::FaceMakerExtrusion
  LengthFwd = 0
  LengthRev = 0
  Solid = false
  Symmetric = false
FEATURE [Part::Cut] Cut002
  Base = -> Cylinder002
  Refine = true
  Tool = -> Extrude003
FEATURE [Part::Feature] Face001
  shape: bbox 18.03 x 18.03 x 2e-07 mm, 1 faces, 0 solids (baked)
FEATURE [Part::Extrusion] Extrude004
  Base = -> Face001
  Dir = (0,0,6)
  DirMode = 0
  FaceMakerClass = Part::FaceMakerExtrusion
  LengthFwd = 0
  LengthRev = 0
  Solid = false
  Symmetric = false
FEATURE [Part::Cut] Cut001
  Base = -> Cylinder850
  Refine = true
  Tool = -> Extrude004
FEATURE [Part::Cylinder] Cylinder005
  Angle = 32.74
  AttacherType = Attacher::AttachEngine3D
  Height = 2.5
  Radius = 10
FEATURE [Part::Cylinder] Cylinder006
  Angle = 32.74
  AttacherType = Attacher::AttachEngine3D
  Height = 2.5
  Radius = 6.9
FEATURE [Part::Cut] Cut004
  Base = -> Cylinder005
  Placement = pos=(0,0,-2.5) rot=(0,0,1;0.244346rad)
  Refine = true
  Tool = -> Cylinder006
FEATURE [Part::Fillet] Fillet001
  Base = -> Cut004
  Edges = 4 edges r=1.2: [Edge2,Edge4,Edge9,Edge12]
  Placement = pos=(0,0,8.5) rot=(0,0,1;0rad)
FEATURE [Part::MultiFuse] Fusion001
  Placement = pos=(0,0,0) rot=(0,0,1;1.0472rad)
  Refine = true
  Shapes = -> [Fillet001,Fillet004,Fillet005]
FEATURE [Part::MultiFuse] Fusion005
  Refine = true
  Shapes = -> [Cut002,Fusion001]
FEATURE [Part::Cylinder] Cylinder007
  Angle = 32.74
  AttacherType = Attacher::AttachEngine3D
  Height = 2.5
  Radius = 10.5
FEATURE [Part::Cylinder] Cylinder008
  Angle = 32.74
  AttacherType = Attacher::AttachEngine3D
  Height = 2.5
  Radius = 7.1
FEATURE [Part::Cut] Cut005
  Base = -> Cylinder007
  Placement = pos=(0,0,-2.5) rot=(0,0,1;0.244346rad)
  Refine = true
  Tool = -> Cylinder008
FEATURE [Part::Fillet] Fillet002
  Base = -> Cut005
  Edges = 4 edges r=1.5: [Edge2,Edge4,Edge9,Edge12]
  Placement = pos=(0,0,0) rot=(0,0,1;2.0944rad)
FEATURE [Part::Cylinder] Cylinder003
  Angle = 32.74
  AttacherType = Attacher::AttachEngine3D
  Height = 2.5
  Radius = 10.5
FEATURE [Part::Cylinder] Cylinder004
  Angle = 32.74
  AttacherType = Attacher::AttachEngine3D
  Height = 2.5
  Radius = 7.1
FEATURE [Part::Cut] Cut003
  Base = -> Cylinder003
  Placement = pos=(0,0,-2.5) rot=(0,0,1;0.244346rad)
  Refine = true
  Tool = -> Cylinder004
FEATURE [Part::Fillet] Fillet007069
  Base = -> Cut003
  Edges = 4 edges r=1.5: [Edge2,Edge4,Edge9,Edge12]
FEATURE [Part::MultiFuse] Fusion626
  Refine = true
  Shapes = -> [Fillet003,Fillet002,Fillet007069]
FEATURE [Part::MultiFuse] Fusion004
  Refine = true
  Shapes = -> [Cut001,Fusion626]
FEATURE [Part::Cut] Cut012
  Base = -> Fusion004
  Refine = true
  Tool = -> Fusion002
FEATURE [Part::MultiFuse] Fusion014
  Placement = pos=(116,85,5) rot=(0,1,0;1.5708rad)
  Refine = true
  Shapes = -> [Fusion005,Cut014195,Cut012]
FEATURE [Part::Cylinder] Cylinder852  label="rod-01"
  Angle = 360
  AttacherType = Attacher::AttachEngine3D
  Height = 65
  Placement = pos=(31,89,23) rot=(0,1,0;1.5708rad)
  Radius = 1.5
FEATURE [Part::Cylinder] Cylinder853  label="exit-shaft"
  Angle = 360
  AttacherType = Attacher::AttachEngine3D
  Height = 58
  Placement = pos=(81,85,5.5) rot=(0,1,0;1.5708rad)
  Radius = 2.5
FEATURE [Part::MultiFuse] Fusion627  label="main-motor"
  Refine = true
  Shapes = -> [Cylinder798,Cylinder852]
FEATURE [Part::Cylinder] Cylinder854  label="secondary-shaft"
  Angle = 360
  AttacherType = Attacher::AttachEngine3D
  Height = 52
  Placement = pos=(81,70,23) rot=(0,1,0;1.5708rad)
  Radius = 2.5
